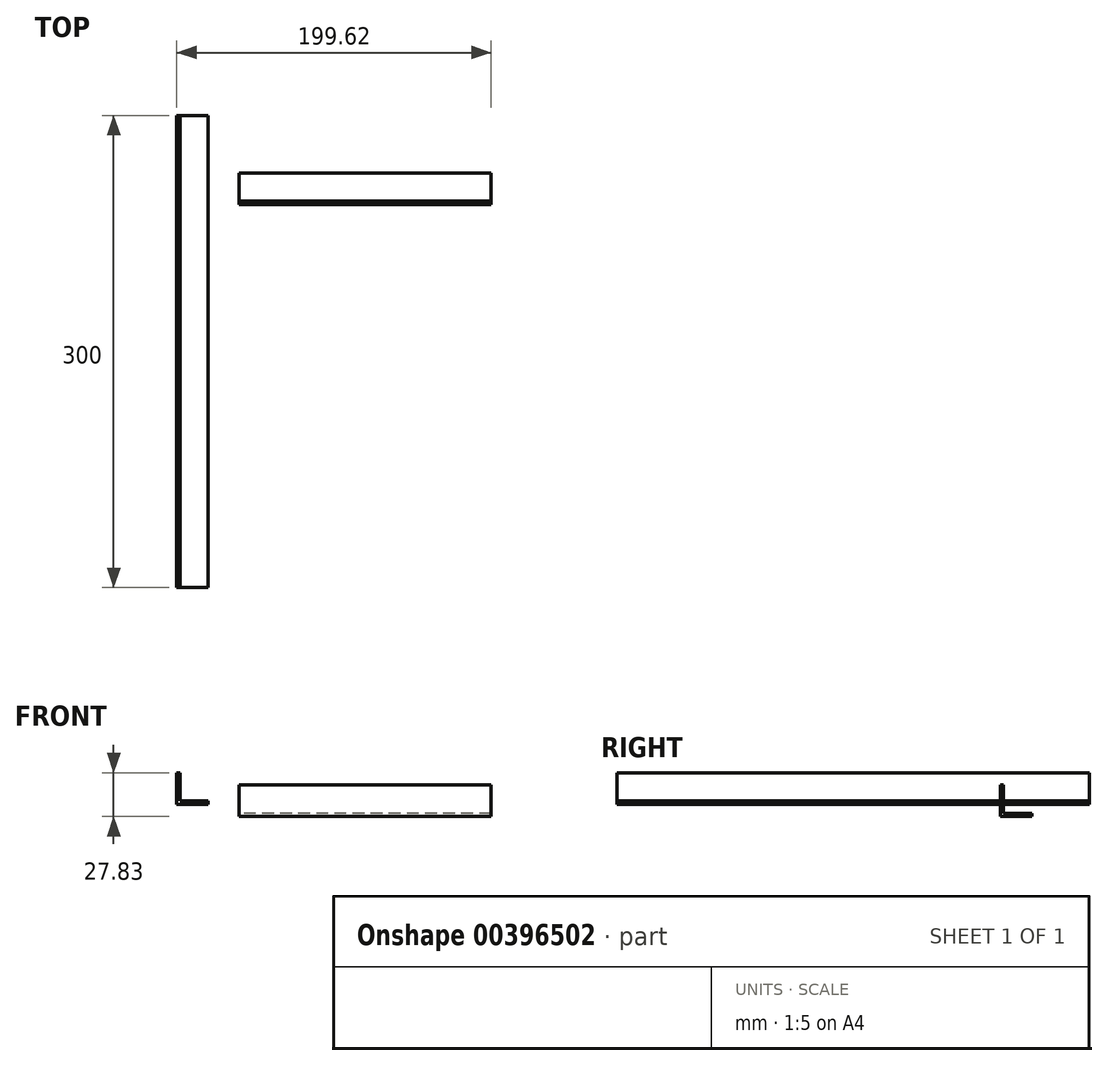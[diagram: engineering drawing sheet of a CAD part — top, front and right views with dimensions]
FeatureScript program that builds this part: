
annotation { "Feature Type Name" : "Feature", "Feature Type Description" : "" }
export const myFeature = defineFeature(function(context is Context, id is Id, definition is map)
    precondition{}
    {
        {
            var Q0;
            Q0=qCreatedBy(makeId("Front.planeOp"),FACE);
            var sketch = newSketch(context, id + "F0", { "sketchPlane" : qUnion([Q0])});
            skLineSegment(sketch, "E0", {"start": v(-39.62, 12.84) * mm, "end": v(-39.62, -7.16) * mm});
            skLineSegment(sketch, "E1", {"start": v(-39.62, -7.16) * mm, "end": v(-19.62, -7.16) * mm});
            skLineSegment(sketch, "E2", {"start": v(-19.62, -7.16) * mm, "end": v(-19.62, -5.16) * mm});
            skLineSegment(sketch, "E3", {"start": v(-19.62, -5.16) * mm, "end": v(-37.62, -5.16) * mm});
            skLineSegment(sketch, "E4", {"start": v(-37.62, -5.16) * mm, "end": v(-37.62, 12.84) * mm});
            skLineSegment(sketch, "E5", {"start": v(-37.62, 12.84) * mm, "end": v(-39.62, 12.84) * mm});
            skSolve(sketch);
        }
        {
            var Q0;
            Q0 = qSketchRegion(id + "F0", true);
            extrude(context, id + "F1", {"entities" : qUnion([Q0]), "depth" : 300 * mm});
        }
        {
            var Q0;
            Q0=qCreatedBy(makeId("Right.planeOp"),FACE);
            var sketch = newSketch(context, id + "F2", { "sketchPlane" : qUnion([Q0])});
            skLineSegment(sketch, "E6", {"start": v(-36.55, -12.99) * mm, "end": v(-54.53, -12.99) * mm});
            skLineSegment(sketch, "E7", {"start": v(-54.53, -12.99) * mm, "end": v(-54.53, 5.01) * mm});
            skLineSegment(sketch, "E8", {"start": v(-54.53, 5.01) * mm, "end": v(-56.53, 5.01) * mm});
            skLineSegment(sketch, "E9", {"start": v(-56.53, 5.01) * mm, "end": v(-56.53, -14.99) * mm});
            skLineSegment(sketch, "E10", {"start": v(-56.53, -14.99) * mm, "end": v(-36.53, -14.99) * mm});
            skLineSegment(sketch, "E11", {"start": v(-36.53, -14.99) * mm, "end": v(-36.55, -12.99) * mm});
            skSolve(sketch);
        }
        {
            var Q0;
            Q0 = qSketchRegion(id + "F2", true);
            extrude(context, id + "F3", {"entities" : qUnion([Q0]), "depth" : 160 * mm});
        }
    });
